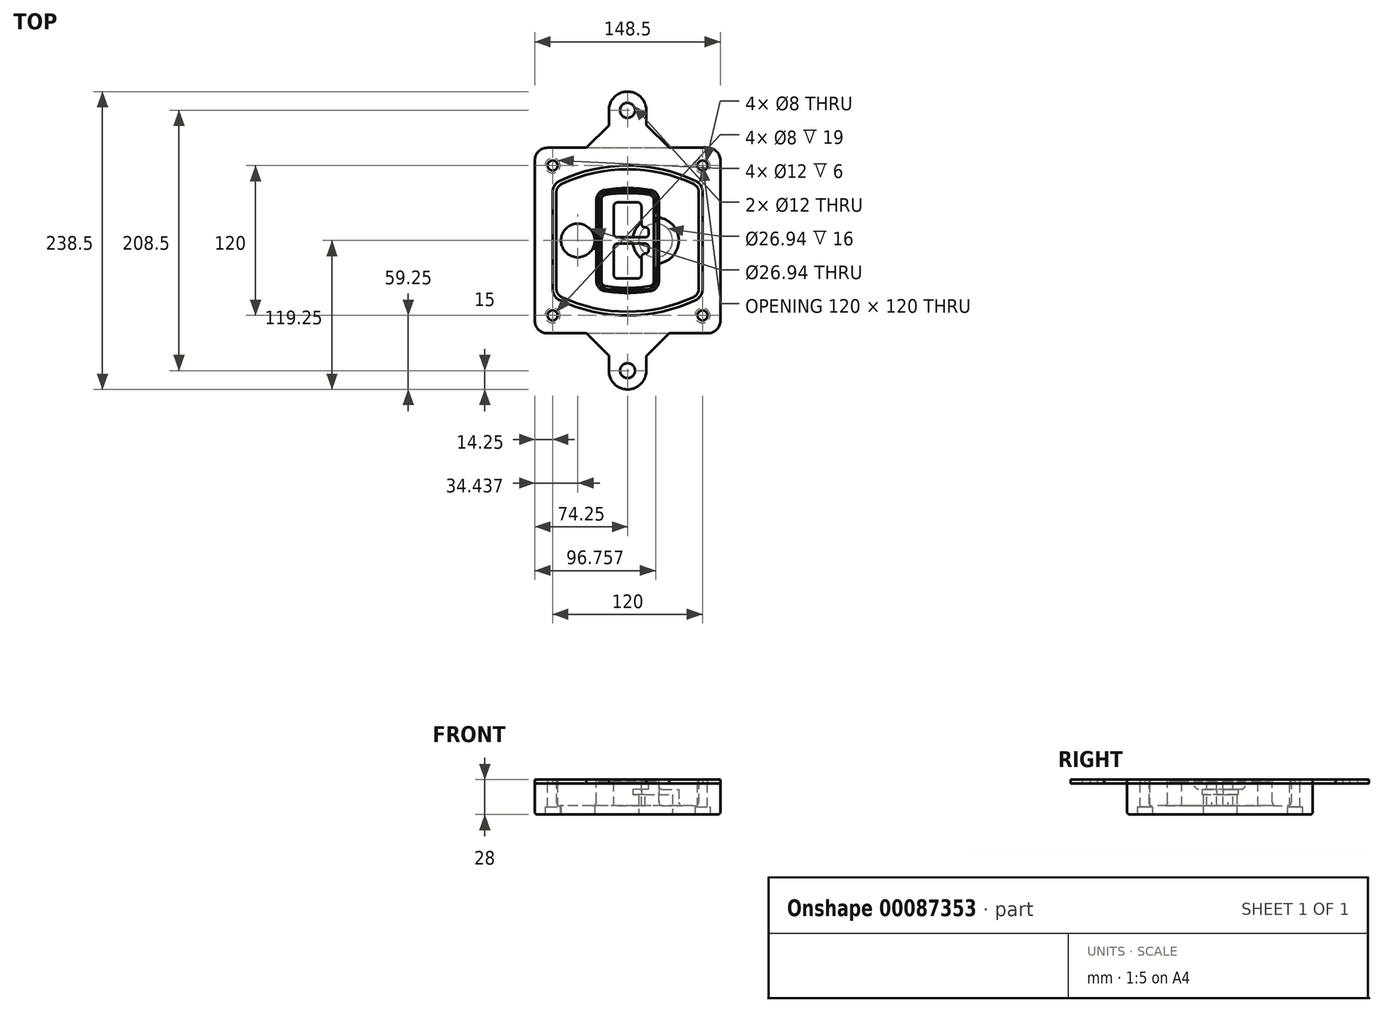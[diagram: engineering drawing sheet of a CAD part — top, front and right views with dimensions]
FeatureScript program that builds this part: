
annotation { "Feature Type Name" : "Feature", "Feature Type Description" : "" }
export const myFeature = defineFeature(function(context is Context, id is Id, definition is map)
    precondition{}
    {
        {
            var Q0;
            Q0=qCreatedBy(makeId("Top.planeOp"),FACE);
            var sketch = newSketch(context, id + "F0", { "sketchPlane" : qUnion([Q0])});
            skPoint(sketch, "E0.rect.middle", {"position": v(0, 0) * mm});
            skLineSegment(sketch, "E1.bottom", {"start": v(-64.25, -74.25) * mm, "end": v(64.25, -74.25) * mm});
            skLineSegment(sketch, "E1.top", {"start": v(-64.25, 74.25) * mm, "end": v(64.25, 74.25) * mm});
            skLineSegment(sketch, "E1.left", {"start": v(-74.25, -64.25) * mm, "end": v(-74.25, 64.25) * mm});
            skLineSegment(sketch, "E1.right", {"start": v(74.25, -64.25) * mm, "end": v(74.25, 64.25) * mm});
            skLineSegment(sketch, "E2", {"start": v(-74.25, 74.25) * mm, "end": v(74.25, -74.25) * mm, "construction": true});
            skLineSegment(sketch, "E3", {"start": v(74.25, 74.25) * mm, "end": v(-74.25, -74.25) * mm, "construction": true});
            skCircle(sketch, "E4", {"center": v(-60, 60) * mm, "radius": 4 * mm});
            skCircle(sketch, "E5", {"center": v(60, 60) * mm, "radius": 4 * mm});
            skCircle(sketch, "E6", {"center": v(60, -60) * mm, "radius": 4 * mm});
            skCircle(sketch, "E7", {"center": v(-60, -60) * mm, "radius": 4 * mm});
            skLineSegment(sketch, "E8", {"start": v(-60, 60) * mm, "end": v(60, 60) * mm, "construction": true});
            skLineSegment(sketch, "E9", {"start": v(60, 60) * mm, "end": v(60, -60) * mm, "construction": true});
            skLineSegment(sketch, "E10", {"start": v(60, -60) * mm, "end": v(-60, -60) * mm, "construction": true});
            skLineSegment(sketch, "E11", {"start": v(-60, -60) * mm, "end": v(-60, 60) * mm, "construction": true});
            skLineSegment(sketch, "E12", {"start": v(-60, 38.83) * mm, "end": v(-60, -38.83) * mm});
            skLineSegment(sketch, "E13", {"start": v(60, 38.83) * mm, "end": v(60, -38.83) * mm});
            skArc(sketch, "E14", {"start": v(54.26, 47.88) * mm, "mid": v(0, 60) * mm, "end": v(-54.26, 47.88) * mm});
            skArc(sketch, "E15", {"start": v(-54.26, -47.88) * mm, "mid": v(0, -60) * mm, "end": v(54.26, -47.88) * mm});
            skLineSegment(sketch, "E16", {"start": v(-60, 0) * mm, "end": v(60, 0) * mm, "construction": true});
            skPoint(sketch, "E17.visualSharp", {"position": v(-60, -45) * mm});
            skArc(sketch, "E17.filletArc", {"start": v(-60, -38.83) * mm, "mid": v(-58.44, -44.2) * mm, "end": v(-54.26, -47.88) * mm});
            skPoint(sketch, "E18.visualSharp", {"position": v(-60, 45) * mm});
            skArc(sketch, "E18.filletArc", {"start": v(-54.26, 47.88) * mm, "mid": v(-58.44, 44.2) * mm, "end": v(-60, 38.83) * mm});
            skPoint(sketch, "E19.visualSharp", {"position": v(60, 45) * mm});
            skArc(sketch, "E19.filletArc", {"start": v(60, 38.83) * mm, "mid": v(58.44, 44.2) * mm, "end": v(54.26, 47.88) * mm});
            skPoint(sketch, "E20.visualSharp", {"position": v(60, -45) * mm});
            skArc(sketch, "E20.filletArc", {"start": v(54.26, -47.88) * mm, "mid": v(58.44, -44.2) * mm, "end": v(60, -38.83) * mm});
            skPoint(sketch, "E21.visualSharp", {"position": v(-74.25, 74.25) * mm});
            skArc(sketch, "E21.filletArc", {"start": v(-64.25, 74.25) * mm, "mid": v(-71.32, 71.32) * mm, "end": v(-74.25, 64.25) * mm});
            skPoint(sketch, "E22.visualSharp", {"position": v(74.25, 74.25) * mm});
            skArc(sketch, "E22.filletArc", {"start": v(74.25, 64.25) * mm, "mid": v(71.32, 71.32) * mm, "end": v(64.25, 74.25) * mm});
            skPoint(sketch, "E23.visualSharp", {"position": v(74.25, -74.25) * mm});
            skArc(sketch, "E23.filletArc", {"start": v(64.25, -74.25) * mm, "mid": v(71.32, -71.32) * mm, "end": v(74.25, -64.25) * mm});
            skPoint(sketch, "E24.visualSharp", {"position": v(-74.25, -74.25) * mm});
            skArc(sketch, "E24.filletArc", {"start": v(-74.25, -64.25) * mm, "mid": v(-71.32, -71.32) * mm, "end": v(-64.25, -74.25) * mm});
            skArc(sketch, "E25.0", {"start": v(57, 38.83) * mm, "mid": v(55.9, 42.58) * mm, "end": v(52.98, 45.17) * mm});
            skLineSegment(sketch, "E25.1", {"start": v(57, 38.83) * mm, "end": v(57, -38.83) * mm});
            skArc(sketch, "E25.2", {"start": v(52.98, -45.17) * mm, "mid": v(55.9, -42.58) * mm, "end": v(57, -38.83) * mm});
            skArc(sketch, "E25.3", {"start": v(-52.98, -45.17) * mm, "mid": v(0, -57) * mm, "end": v(52.98, -45.17) * mm});
            skArc(sketch, "E25.4", {"start": v(-57, -38.83) * mm, "mid": v(-55.9, -42.58) * mm, "end": v(-52.98, -45.17) * mm});
            skArc(sketch, "E25.5", {"start": v(52.98, 45.17) * mm, "mid": v(0, 57) * mm, "end": v(-52.98, 45.17) * mm});
            skLineSegment(sketch, "E25.6", {"start": v(-57, 38.83) * mm, "end": v(-57, -38.83) * mm});
            skArc(sketch, "E25.7", {"start": v(-52.98, 45.17) * mm, "mid": v(-55.9, 42.58) * mm, "end": v(-57, 38.83) * mm});
            skArc(sketch, "E26.0", {"start": v(-55.96, 51.5) * mm, "mid": v(-61.82, 46.33) * mm, "end": v(-64, 38.83) * mm});
            skArc(sketch, "E26.1", {"start": v(55.96, 51.5) * mm, "mid": v(0, 64) * mm, "end": v(-55.96, 51.5) * mm});
            skArc(sketch, "E26.2", {"start": v(64, 38.83) * mm, "mid": v(61.82, 46.33) * mm, "end": v(55.96, 51.5) * mm});
            skLineSegment(sketch, "E26.3", {"start": v(64, 38.83) * mm, "end": v(64, -38.83) * mm});
            skArc(sketch, "E26.4", {"start": v(55.96, -51.5) * mm, "mid": v(61.82, -46.33) * mm, "end": v(64, -38.83) * mm});
            skLineSegment(sketch, "E26.5", {"start": v(-64, 38.83) * mm, "end": v(-64, -38.83) * mm});
            skArc(sketch, "E26.6", {"start": v(-55.96, -51.5) * mm, "mid": v(0, -64) * mm, "end": v(55.96, -51.5) * mm});
            skArc(sketch, "E26.7", {"start": v(-64, -38.83) * mm, "mid": v(-61.82, -46.33) * mm, "end": v(-55.96, -51.5) * mm});
            skSolve(sketch);
        }
        {
            var Q0;
            Q0=makeQuery(id+"F0.imprint","IMPRINT",FACE,{"disambiguationData":[TD([[makeQuery(id+"F0.imprint","IMPRINT",EDGE,{"derivedFrom":sQuery(id+"F0.wireOp",EDGE,"E1.bottom")}),1.0]])]});
            var Q1;
            Q1=makeQuery(id+"F0.imprint","IMPRINT",FACE,{"disambiguationData":[TD([[makeQuery(id+"F0.imprint","IMPRINT",EDGE,{"derivedFrom":sQuery(id+"F0.wireOp",EDGE,"E12")}),1.0]])]});
            var Q2;
            Q2=makeQuery(id+"F0.imprint","IMPRINT",FACE,{"disambiguationData":[TD([[makeQuery(id+"F0.imprint","IMPRINT",EDGE,{"derivedFrom":sQuery(id+"F0.wireOp",EDGE,"E25.0")}),1.0]])]});
            var Q3;
            Q3=makeQuery(id+"F0.imprint","IMPRINT",FACE,{"disambiguationData":[TD([[makeQuery(id+"F0.imprint","IMPRINT",EDGE,{"derivedFrom":sQuery(id+"F0.wireOp",EDGE,"E12")}),-1.0]])]});
            extrude(context, id + "F1", {"entities" : qUnion([Q0, Q1, Q2, Q3]), "oppositeDirection" : true, "depth" : 25 * mm});
        }
        {
            var Q0;
            Q0=makeQuery(id+"F0.imprint","IMPRINT",FACE,{"disambiguationData":[TD([[makeQuery(id+"F0.imprint","IMPRINT",EDGE,{"derivedFrom":sQuery(id+"F0.wireOp",EDGE,"E12")}),1.0]])]});
            extrude(context, id + "F2", {"entities" : qUnion([Q0]), "operationType" : NewBodyOperationType.ADD, "depth" : 3 * mm});
        }
        {
            var Q0;
            Q0=makeQuery(id+"F0.imprint","IMPRINT",FACE,{"disambiguationData":[TD([[makeQuery(id+"F0.imprint","IMPRINT",EDGE,{"derivedFrom":sQuery(id+"F0.wireOp",EDGE,"E25.0")}),1.0]])]});
            extrude(context, id + "F3", {"entities" : qUnion([Q0]), "operationType" : NewBodyOperationType.REMOVE, "oppositeDirection" : true, "depth" : 18 * mm});
        }
        {
            var Q0;
            Q0=makeQuery(id+"F2.opExtrude","CAP_FACE",FACE,{"disambiguationData":[OSD([sQuery(id+"F0.wireOp",EDGE,"E12"),sQuery(id+"F0.wireOp",EDGE,"E13"),sQuery(id+"F0.wireOp",EDGE,"E14"),sQuery(id+"F0.wireOp",EDGE,"E15"),sQuery(id+"F0.wireOp",EDGE,"E17.filletArc"),sQuery(id+"F0.wireOp",EDGE,"E18.filletArc"),sQuery(id+"F0.wireOp",EDGE,"E19.filletArc"),sQuery(id+"F0.wireOp",EDGE,"E20.filletArc"),sQuery(id+"F0.wireOp",EDGE,"E25.0"),sQuery(id+"F0.wireOp",EDGE,"E25.1"),sQuery(id+"F0.wireOp",EDGE,"E25.2"),sQuery(id+"F0.wireOp",EDGE,"E25.3"),sQuery(id+"F0.wireOp",EDGE,"E25.4"),sQuery(id+"F0.wireOp",EDGE,"E25.5"),sQuery(id+"F0.wireOp",EDGE,"E25.6"),sQuery(id+"F0.wireOp",EDGE,"E25.7")])],"isStart":false});
            var sketch = newSketch(context, id + "F4", { "sketchPlane" : qUnion([Q0])});
            skArc(sketch, "E27.0", {"start": v(-18.34, -40.45) * mm, "mid": v(0, -42) * mm, "end": v(18.34, -40.45) * mm});
            skArc(sketch, "E28.0", {"start": v(18.34, 40.45) * mm, "mid": v(0, 42) * mm, "end": v(-18.34, 40.45) * mm});
            skLineSegment(sketch, "E29", {"start": v(-25, 32.57) * mm, "end": v(-25, -32.57) * mm});
            skLineSegment(sketch, "E30", {"start": v(25, 32.57) * mm, "end": v(25, -32.57) * mm});
            skLineSegment(sketch, "E31", {"start": v(-25, 39.1) * mm, "end": v(25, 39.1) * mm, "construction": true});
            skLineSegment(sketch, "E32", {"start": v(-25, -39.1) * mm, "end": v(25, -39.1) * mm, "construction": true});
            skPoint(sketch, "E33.visualSharp", {"position": v(-25, 39.1) * mm});
            skArc(sketch, "E33.filletArc", {"start": v(-18.34, 40.45) * mm, "mid": v(-23.11, 37.73) * mm, "end": v(-25, 32.57) * mm});
            skPoint(sketch, "E34.visualSharp", {"position": v(25, 39.1) * mm});
            skArc(sketch, "E34.filletArc", {"start": v(25, 32.57) * mm, "mid": v(23.11, 37.73) * mm, "end": v(18.34, 40.45) * mm});
            skPoint(sketch, "E35.visualSharp", {"position": v(25, -39.1) * mm});
            skArc(sketch, "E35.filletArc", {"start": v(18.34, -40.45) * mm, "mid": v(23.11, -37.73) * mm, "end": v(25, -32.57) * mm});
            skPoint(sketch, "E36.visualSharp", {"position": v(-25, -39.1) * mm});
            skArc(sketch, "E36.filletArc", {"start": v(-25, -32.57) * mm, "mid": v(-23.11, -37.73) * mm, "end": v(-18.34, -40.45) * mm});
            skArc(sketch, "E37.0", {"start": v(52.98, 45.17) * mm, "mid": v(0, 57) * mm, "end": v(-52.98, 45.17) * mm});
            skArc(sketch, "E37.1", {"start": v(-52.98, 45.17) * mm, "mid": v(-55.9, 42.58) * mm, "end": v(-57, 38.83) * mm});
            skLineSegment(sketch, "E37.2", {"start": v(-57, 38.83) * mm, "end": v(-57, -38.83) * mm});
            skArc(sketch, "E37.3", {"start": v(-57, -38.83) * mm, "mid": v(-55.9, -42.58) * mm, "end": v(-52.98, -45.17) * mm});
            skArc(sketch, "E37.4", {"start": v(-52.98, -45.17) * mm, "mid": v(0, -57) * mm, "end": v(52.98, -45.17) * mm});
            skArc(sketch, "E37.5", {"start": v(52.98, -45.17) * mm, "mid": v(55.9, -42.58) * mm, "end": v(57, -38.83) * mm});
            skLineSegment(sketch, "E37.6", {"start": v(57, 38.83) * mm, "end": v(57, -38.83) * mm});
            skArc(sketch, "E37.7", {"start": v(57, 38.83) * mm, "mid": v(55.9, 42.58) * mm, "end": v(52.98, 45.17) * mm});
            skLineSegment(sketch, "E38.0", {"start": v(23, 32.57) * mm, "end": v(23, -32.57) * mm});
            skArc(sketch, "E38.1", {"start": v(18, -38.48) * mm, "mid": v(21.58, -36.44) * mm, "end": v(23, -32.57) * mm});
            skArc(sketch, "E38.2", {"start": v(-18, -38.48) * mm, "mid": v(0, -40) * mm, "end": v(18, -38.48) * mm});
            skArc(sketch, "E38.3", {"start": v(-23, -32.57) * mm, "mid": v(-21.58, -36.44) * mm, "end": v(-18, -38.48) * mm});
            skLineSegment(sketch, "E38.4", {"start": v(-23, 32.57) * mm, "end": v(-23, -32.57) * mm});
            skArc(sketch, "E38.5", {"start": v(23, 32.57) * mm, "mid": v(21.58, 36.44) * mm, "end": v(18, 38.48) * mm});
            skArc(sketch, "E38.6", {"start": v(-18, 38.48) * mm, "mid": v(-21.58, 36.44) * mm, "end": v(-23, 32.57) * mm});
            skArc(sketch, "E38.7", {"start": v(18, 38.48) * mm, "mid": v(0, 40) * mm, "end": v(-18, 38.48) * mm});
            skArc(sketch, "E39.0", {"start": v(21, 32.57) * mm, "mid": v(20.06, 35.15) * mm, "end": v(17.67, 36.5) * mm});
            skLineSegment(sketch, "E39.1", {"start": v(21, 32.57) * mm, "end": v(21, -32.57) * mm});
            skArc(sketch, "E39.2", {"start": v(17.67, -36.5) * mm, "mid": v(20.06, -35.15) * mm, "end": v(21, -32.57) * mm});
            skArc(sketch, "E39.3", {"start": v(-17.67, -36.5) * mm, "mid": v(0, -38) * mm, "end": v(17.67, -36.5) * mm});
            skArc(sketch, "E39.4", {"start": v(-21, -32.57) * mm, "mid": v(-20.06, -35.15) * mm, "end": v(-17.67, -36.5) * mm});
            skArc(sketch, "E39.5", {"start": v(17.67, 36.5) * mm, "mid": v(0, 38) * mm, "end": v(-17.67, 36.5) * mm});
            skLineSegment(sketch, "E39.6", {"start": v(-21, 32.57) * mm, "end": v(-21, -32.57) * mm});
            skArc(sketch, "E39.7", {"start": v(-17.67, 36.5) * mm, "mid": v(-20.06, 35.15) * mm, "end": v(-21, 32.57) * mm});
            skLineSegment(sketch, "E40", {"start": v(-25, 0) * mm, "end": v(25, 0) * mm, "construction": true});
            skLineSegment(sketch, "E41", {"start": v(-11, 5.5) * mm, "end": v(-11, 27.5) * mm});
            skLineSegment(sketch, "E42", {"start": v(-8, 30.5) * mm, "end": v(8, 30.5) * mm});
            skLineSegment(sketch, "E43", {"start": v(11, 27.5) * mm, "end": v(11, 13.5) * mm});
            skLineSegment(sketch, "E44", {"start": v(14, 10.5) * mm, "end": v(14, 10.5) * mm});
            skLineSegment(sketch, "E45", {"start": v(17, 7.5) * mm, "end": v(17, 5.5) * mm});
            skLineSegment(sketch, "E46", {"start": v(14, 2.5) * mm, "end": v(-8, 2.5) * mm});
            skPoint(sketch, "E47.visualSharp", {"position": v(-11, 30.5) * mm});
            skArc(sketch, "E47.filletArc", {"start": v(-8, 30.5) * mm, "mid": v(-10.12, 29.62) * mm, "end": v(-11, 27.5) * mm});
            skPoint(sketch, "E48.visualSharp", {"position": v(11, 30.5) * mm});
            skArc(sketch, "E48.filletArc", {"start": v(11, 27.5) * mm, "mid": v(10.12, 29.62) * mm, "end": v(8, 30.5) * mm});
            skPoint(sketch, "E49.visualSharp", {"position": v(11, 10.5) * mm});
            skArc(sketch, "E49.filletArc", {"start": v(11, 13.5) * mm, "mid": v(11.88, 11.38) * mm, "end": v(14, 10.5) * mm});
            skPoint(sketch, "E50.visualSharp", {"position": v(17, 10.5) * mm});
            skArc(sketch, "E50.filletArc", {"start": v(17, 7.5) * mm, "mid": v(16.12, 9.62) * mm, "end": v(14, 10.5) * mm});
            skPoint(sketch, "E51.visualSharp", {"position": v(17, 2.5) * mm});
            skArc(sketch, "E51.filletArc", {"start": v(14, 2.5) * mm, "mid": v(16.12, 3.38) * mm, "end": v(17, 5.5) * mm});
            skPoint(sketch, "E52.visualSharp", {"position": v(-11, 2.5) * mm});
            skArc(sketch, "E52.filletArc", {"start": v(-11, 5.5) * mm, "mid": v(-10.12, 3.38) * mm, "end": v(-8, 2.5) * mm});
            skLineSegment(sketch, "E53.0.MirrorCS", {"start": v(14, -2.5) * mm, "end": v(-8, -2.5) * mm});
            skArc(sketch, "E54.0.MirrorCS", {"start": v(-11, -5.5) * mm, "mid": v(-10.12, -3.38) * mm, "end": v(-8, -2.5) * mm});
            skLineSegment(sketch, "E55.0.MirrorCS", {"start": v(-11, -5.5) * mm, "end": v(-11, -27.5) * mm});
            skArc(sketch, "E56.0.MirrorCS", {"start": v(-8, -30.5) * mm, "mid": v(-10.12, -29.62) * mm, "end": v(-11, -27.5) * mm});
            skLineSegment(sketch, "E57.0.MirrorCS", {"start": v(-8, -30.5) * mm, "end": v(8, -30.5) * mm});
            skArc(sketch, "E58.0.MirrorCS", {"start": v(11, -27.5) * mm, "mid": v(10.12, -29.62) * mm, "end": v(8, -30.5) * mm});
            skLineSegment(sketch, "E59.0.MirrorCS", {"start": v(11, -27.5) * mm, "end": v(11, -13.5) * mm});
            skArc(sketch, "E60.0.MirrorCS", {"start": v(11, -13.5) * mm, "mid": v(11.88, -11.38) * mm, "end": v(14, -10.5) * mm});
            skArc(sketch, "E61.0.MirrorCS", {"start": v(17, -7.5) * mm, "mid": v(16.12, -9.62) * mm, "end": v(14, -10.5) * mm});
            skLineSegment(sketch, "E62.0.MirrorCS", {"start": v(17, -7.5) * mm, "end": v(17, -5.5) * mm});
            skArc(sketch, "E63.0.MirrorCS", {"start": v(14, -2.5) * mm, "mid": v(16.12, -3.38) * mm, "end": v(17, -5.5) * mm});
            skSolve(sketch);
        }
        {
            var Q0;
            Q0=makeQuery(id+"F4.imprint","IMPRINT",FACE,{"disambiguationData":[TD([[makeQuery(id+"F4.imprint","IMPRINT",EDGE,{"derivedFrom":sQuery(id+"F4.wireOp",EDGE,"E27.0")}),1.0]])]});
            var Q1;
            Q1=makeQuery(id+"F4.imprint","IMPRINT",FACE,{"disambiguationData":[TD([[makeQuery(id+"F4.imprint","IMPRINT",EDGE,{"derivedFrom":sQuery(id+"F4.wireOp",EDGE,"E38.0")}),-1.0]])]});
            var Q2;
            Q2=makeQuery(id+"F4.imprint","IMPRINT",FACE,{"disambiguationData":[TD([[makeQuery(id+"F4.imprint","IMPRINT",EDGE,{"derivedFrom":sQuery(id+"F4.wireOp",EDGE,"E39.0")}),1.0]])]});
            extrude(context, id + "F5", {"entities" : qUnion([Q0, Q1, Q2]), "operationType" : NewBodyOperationType.ADD, "endBound" : BoundingType.UP_TO_NEXT, "oppositeDirection" : true, "depth" : 25 * mm});
        }
        {
            var Q0;
            Q0=makeQuery(id+"F4.imprint","IMPRINT",FACE,{"disambiguationData":[TD([[makeQuery(id+"F4.imprint","IMPRINT",EDGE,{"derivedFrom":sQuery(id+"F4.wireOp",EDGE,"E38.0")}),-1.0]])]});
            extrude(context, id + "F6", {"entities" : qUnion([Q0]), "operationType" : NewBodyOperationType.REMOVE, "oppositeDirection" : true, "depth" : 2 * mm});
        }
        {
            var Q0;
            Q0=makeQuery(id+"F1.opExtrude","CAP_FACE",FACE,{"disambiguationData":[OSD([sQuery(id+"F0.wireOp",EDGE,"E1.bottom"),sQuery(id+"F0.wireOp",EDGE,"E1.top"),sQuery(id+"F0.wireOp",EDGE,"E1.left"),sQuery(id+"F0.wireOp",EDGE,"E1.right"),sQuery(id+"F0.wireOp",EDGE,"E4"),sQuery(id+"F0.wireOp",EDGE,"E5"),sQuery(id+"F0.wireOp",EDGE,"E6"),sQuery(id+"F0.wireOp",EDGE,"E7"),sQuery(id+"F0.wireOp",EDGE,"E21.filletArc"),sQuery(id+"F0.wireOp",EDGE,"E22.filletArc"),sQuery(id+"F0.wireOp",EDGE,"E23.filletArc"),sQuery(id+"F0.wireOp",EDGE,"E24.filletArc")])],"isStart":false});
            var sketch = newSketch(context, id + "F7", { "sketchPlane" : qUnion([Q0])});
            skCircle(sketch, "E64", {"center": v(22.5, 0) * mm, "radius": 13.47 * mm});
            skCircle(sketch, "E65", {"center": v(-39.81, 0) * mm, "radius": 13.47 * mm});
            skLineSegment(sketch, "E66", {"start": v(74.25, 0) * mm, "end": v(-74.25, 0) * mm});
            skCircle(sketch, "E67", {"center": v(22.5, 0) * mm, "radius": 18.47 * mm});
            skCircle(sketch, "E68", {"center": v(60, -60) * mm, "radius": 6 * mm});
            skCircle(sketch, "E69", {"center": v(-60, -60) * mm, "radius": 6 * mm});
            skCircle(sketch, "E70", {"center": v(-60, 60) * mm, "radius": 6 * mm});
            skCircle(sketch, "E71", {"center": v(60, 60) * mm, "radius": 6 * mm});
            skSolve(sketch);
        }
        {
            var Q0;
            {var subQ1=sQuery(id+"F7.wireOp",EDGE,"E66");var subQ4=sQuery(id+"F7.wireOp",EDGE,"E64");var subQ6=makeQuery(id+"F7.imprint","INTERSECT",VERTEX,{"disambiguationData":[OD(0.0)],"derivedFrom":[subQ4,subQ1]});Q0=makeQuery(id+"F7.imprint","IMPRINT",FACE,{"disambiguationData":[TD([[makeQuery(id+"F7.imprint","IMPRINT",EDGE,{"disambiguationData":[TD([[subQ6,-1.0]])],"derivedFrom":subQ4}),-1.0]])]});}
            var Q1;
            {var subQ0=sQuery(id+"F7.wireOp",EDGE,"E66");var subQ1=sQuery(id+"F7.wireOp",EDGE,"E64");var subQ3=makeQuery(id+"F7.imprint","INTERSECT",VERTEX,{"disambiguationData":[OD(0.0)],"derivedFrom":[subQ1,subQ0]});Q1=makeQuery(id+"F7.imprint","IMPRINT",FACE,{"disambiguationData":[TD([[makeQuery(id+"F7.imprint","IMPRINT",EDGE,{"disambiguationData":[TD([[subQ3,-1.0]])],"derivedFrom":subQ1}),1.0]])]});}
            var Q2;
            {var subQ0=sQuery(id+"F7.wireOp",EDGE,"E66");var subQ1=sQuery(id+"F7.wireOp",EDGE,"E64");var subQ3=makeQuery(id+"F7.imprint","INTERSECT",VERTEX,{"disambiguationData":[OD(0.0)],"derivedFrom":[subQ1,subQ0]});Q2=makeQuery(id+"F7.imprint","IMPRINT",FACE,{"disambiguationData":[TD([[makeQuery(id+"F7.imprint","IMPRINT",EDGE,{"disambiguationData":[TD([[subQ3,1.0]])],"derivedFrom":subQ1}),1.0]])]});}
            var Q3;
            {var subQ1=sQuery(id+"F7.wireOp",EDGE,"E66");var subQ4=sQuery(id+"F7.wireOp",EDGE,"E64");var subQ6=makeQuery(id+"F7.imprint","INTERSECT",VERTEX,{"disambiguationData":[OD(0.0)],"derivedFrom":[subQ4,subQ1]});Q3=makeQuery(id+"F7.imprint","IMPRINT",FACE,{"disambiguationData":[TD([[makeQuery(id+"F7.imprint","IMPRINT",EDGE,{"disambiguationData":[TD([[subQ6,1.0]])],"derivedFrom":subQ4}),-1.0]])]});}
            extrude(context, id + "F8", {"entities" : qUnion([Q0, Q1, Q2, Q3]), "operationType" : NewBodyOperationType.ADD, "oppositeDirection" : true, "depth" : 20 * mm});
        }
        {
            var Q0;
            {var subQ0=sQuery(id+"F7.wireOp",EDGE,"E66");var subQ1=sQuery(id+"F7.wireOp",EDGE,"E64");var subQ3=makeQuery(id+"F7.imprint","INTERSECT",VERTEX,{"disambiguationData":[OD(0.0)],"derivedFrom":[subQ1,subQ0]});Q0=makeQuery(id+"F7.imprint","IMPRINT",FACE,{"disambiguationData":[TD([[makeQuery(id+"F7.imprint","IMPRINT",EDGE,{"disambiguationData":[TD([[subQ3,-1.0]])],"derivedFrom":subQ1}),1.0]])]});}
            var Q1;
            {var subQ0=sQuery(id+"F7.wireOp",EDGE,"E66");var subQ1=sQuery(id+"F7.wireOp",EDGE,"E64");var subQ3=makeQuery(id+"F7.imprint","INTERSECT",VERTEX,{"disambiguationData":[OD(0.0)],"derivedFrom":[subQ1,subQ0]});Q1=makeQuery(id+"F7.imprint","IMPRINT",FACE,{"disambiguationData":[TD([[makeQuery(id+"F7.imprint","IMPRINT",EDGE,{"disambiguationData":[TD([[subQ3,1.0]])],"derivedFrom":subQ1}),1.0]])]});}
            extrude(context, id + "F9", {"entities" : qUnion([Q0, Q1]), "operationType" : NewBodyOperationType.REMOVE, "oppositeDirection" : true, "depth" : 16 * mm});
        }
        {
            var Q0;
            {var subQ0=sQuery(id+"F7.wireOp",EDGE,"E66");var subQ1=sQuery(id+"F7.wireOp",EDGE,"E65");var subQ3=makeQuery(id+"F7.imprint","INTERSECT",VERTEX,{"disambiguationData":[OD(0.0)],"derivedFrom":[subQ1,subQ0]});Q0=makeQuery(id+"F7.imprint","IMPRINT",FACE,{"disambiguationData":[TD([[makeQuery(id+"F7.imprint","IMPRINT",EDGE,{"disambiguationData":[TD([[subQ3,-1.0]])],"derivedFrom":subQ1}),1.0]])]});}
            var Q1;
            {var subQ0=sQuery(id+"F7.wireOp",EDGE,"E66");var subQ1=sQuery(id+"F7.wireOp",EDGE,"E65");var subQ3=makeQuery(id+"F7.imprint","INTERSECT",VERTEX,{"disambiguationData":[OD(0.0)],"derivedFrom":[subQ1,subQ0]});Q1=makeQuery(id+"F7.imprint","IMPRINT",FACE,{"disambiguationData":[TD([[makeQuery(id+"F7.imprint","IMPRINT",EDGE,{"disambiguationData":[TD([[subQ3,1.0]])],"derivedFrom":subQ1}),1.0]])]});}
            extrude(context, id + "F10", {"entities" : qUnion([Q0, Q1]), "operationType" : NewBodyOperationType.REMOVE, "oppositeDirection" : true, "depth" : 25 * mm});
        }
        {
            var Q0;
            Q0=makeQuery(id+"F7.imprint","IMPRINT",FACE,{"disambiguationData":[TD([[makeQuery(id+"F7.imprint","IMPRINT",EDGE,{"derivedFrom":sQuery(id+"F7.wireOp",EDGE,"E68")}),1.0]])]});
            var Q1;
            Q1=makeQuery(id+"F7.imprint","IMPRINT",FACE,{"disambiguationData":[TD([[makeQuery(id+"F7.imprint","IMPRINT",EDGE,{"derivedFrom":makeQuery(id+"F1.opExtrude","CAP_EDGE",EDGE,{"disambiguationData":[OSD([sQuery(id+"F0.wireOp",EDGE,"E5")])],"isStart":false})}),-1.0]])]});
            var Q2;
            Q2=makeQuery(id+"F7.imprint","IMPRINT",FACE,{"disambiguationData":[TD([[makeQuery(id+"F7.imprint","IMPRINT",EDGE,{"derivedFrom":sQuery(id+"F7.wireOp",EDGE,"E69")}),1.0]])]});
            var Q3;
            Q3=makeQuery(id+"F7.imprint","IMPRINT",FACE,{"disambiguationData":[TD([[makeQuery(id+"F7.imprint","IMPRINT",EDGE,{"derivedFrom":makeQuery(id+"F1.opExtrude","CAP_EDGE",EDGE,{"disambiguationData":[OSD([sQuery(id+"F0.wireOp",EDGE,"E4")])],"isStart":false})}),-1.0]])]});
            var Q4;
            Q4=makeQuery(id+"F7.imprint","IMPRINT",FACE,{"disambiguationData":[TD([[makeQuery(id+"F7.imprint","IMPRINT",EDGE,{"derivedFrom":sQuery(id+"F7.wireOp",EDGE,"E70")}),1.0]])]});
            var Q5;
            Q5=makeQuery(id+"F7.imprint","IMPRINT",FACE,{"disambiguationData":[TD([[makeQuery(id+"F7.imprint","IMPRINT",EDGE,{"derivedFrom":makeQuery(id+"F1.opExtrude","CAP_EDGE",EDGE,{"disambiguationData":[OSD([sQuery(id+"F0.wireOp",EDGE,"E7")])],"isStart":false})}),-1.0]])]});
            var Q6;
            Q6=makeQuery(id+"F7.imprint","IMPRINT",FACE,{"disambiguationData":[TD([[makeQuery(id+"F7.imprint","IMPRINT",EDGE,{"derivedFrom":sQuery(id+"F7.wireOp",EDGE,"E71")}),1.0]])]});
            var Q7;
            Q7=makeQuery(id+"F7.imprint","IMPRINT",FACE,{"disambiguationData":[TD([[makeQuery(id+"F7.imprint","IMPRINT",EDGE,{"derivedFrom":makeQuery(id+"F1.opExtrude","CAP_EDGE",EDGE,{"disambiguationData":[OSD([sQuery(id+"F0.wireOp",EDGE,"E6")])],"isStart":false})}),-1.0]])]});
            extrude(context, id + "F11", {"entities" : qUnion([Q0, Q1, Q2, Q3, Q4, Q5, Q6, Q7]), "operationType" : NewBodyOperationType.REMOVE, "oppositeDirection" : true, "depth" : 6 * mm});
        }
        {
            var Q0;
            Q0=makeQuery(id+"F9.boolean.opBoolean","COPY",FACE,{"derivedFrom":makeQuery(id+"F9.opExtrude","CAP_FACE",FACE,{"disambiguationData":[OSD([sQuery(id+"F7.wireOp",EDGE,"E64")])],"isStart":false})});
            var sketch = newSketch(context, id + "F12", { "sketchPlane" : qUnion([Q0])});
            skArc(sketch, "E72.0", {"start": v(11, 14.45) * mm, "mid": v(6.45, 9.13) * mm, "end": v(4.2, 2.5) * mm});
            skArc(sketch, "E72.1", {"start": v(4.2, -2.5) * mm, "mid": v(6.45, -9.13) * mm, "end": v(11, -14.45) * mm});
            skLineSegment(sketch, "E73", {"start": v(4.2, -2.5) * mm, "end": v(14, -2.5) * mm});
            skLineSegment(sketch, "E74.0", {"start": v(14, 2.5) * mm, "end": v(4.2, 2.5) * mm});
            skArc(sketch, "E74.1", {"start": v(14, 2.5) * mm, "mid": v(16.12, 3.38) * mm, "end": v(17, 5.5) * mm});
            skLineSegment(sketch, "E74.2", {"start": v(17, 7.5) * mm, "end": v(17, 5.5) * mm});
            skArc(sketch, "E74.3", {"start": v(17, 7.5) * mm, "mid": v(16.12, 9.62) * mm, "end": v(14, 10.5) * mm});
            skArc(sketch, "E74.4", {"start": v(11, 13.5) * mm, "mid": v(11.88, 11.38) * mm, "end": v(14, 10.5) * mm});
            skLineSegment(sketch, "E74.5", {"start": v(11, 14.45) * mm, "end": v(11, 13.5) * mm});
            skLineSegment(sketch, "E74.7", {"start": v(14, -2.5) * mm, "end": v(4.2, -2.5) * mm});
            skArc(sketch, "E74.8", {"start": v(14, -2.5) * mm, "mid": v(16.12, -3.38) * mm, "end": v(17, -5.5) * mm});
            skLineSegment(sketch, "E74.9", {"start": v(17, -7.5) * mm, "end": v(17, -5.5) * mm});
            skArc(sketch, "E74.10", {"start": v(17, -7.5) * mm, "mid": v(16.12, -9.62) * mm, "end": v(14, -10.5) * mm});
            skArc(sketch, "E74.11", {"start": v(11, -13.5) * mm, "mid": v(11.88, -11.38) * mm, "end": v(14, -10.5) * mm});
            skLineSegment(sketch, "E74.12", {"start": v(11, -14.45) * mm, "end": v(11, -13.5) * mm});
            skPoint(sketch, "E75.orphan", {"position": v(11, -27.5) * mm});
            skPoint(sketch, "E76.orphan", {"position": v(-8, -2.5) * mm});
            skPoint(sketch, "E77.orphan", {"position": v(-8, 2.5) * mm});
            skPoint(sketch, "E78.orphan", {"position": v(11, 27.5) * mm});
            skSolve(sketch);
        }
        {
            var Q0;
            {var subQ7=sQuery(id+"F12.wireOp",EDGE,"E72.0");var subQ14=sQuery(id+"F12.wireOp",EDGE,"E72.1");var subQ16=sQuery(id+"F12.wireOp",EDGE,"E74.1");var subQ18=sQuery(id+"F12.wireOp",EDGE,"E74.8");Q0=qUnion([makeQuery(id+"F12.imprint","IMPRINT",FACE,{"disambiguationData":[TD([[makeQuery(id+"F12.imprint","IMPRINT",EDGE,{"derivedFrom":subQ7}),1.0]])]}),makeQuery(id+"F12.imprint","IMPRINT",FACE,{"disambiguationData":[TD([[makeQuery(id+"F12.imprint","IMPRINT",EDGE,{"derivedFrom":subQ14}),1.0]])]}),makeQuery(id+"F12.imprint","IMPRINT",FACE,{"disambiguationData":[TD([[makeQuery(id+"F12.imprint","IMPRINT",EDGE,{"derivedFrom":subQ16}),1.0]])]}),makeQuery(id+"F12.imprint","IMPRINT",FACE,{"disambiguationData":[TD([[makeQuery(id+"F12.imprint","IMPRINT",EDGE,{"derivedFrom":subQ18}),-1.0]])]})]);}
            var Q1;
            Q1=makeQuery(id+"F5.boolean.opBoolean","SPLIT",FACE,{"disambiguationData":[TD([makeQuery(id+"F5.opExtrude","SWEPT_FACE",FACE,{"disambiguationData":[OSD([sQuery(id+"F4.wireOp",EDGE,"E41")])]})])],"derivedFrom":makeQuery(id+"F3.boolean.opBoolean","COPY",FACE,{"derivedFrom":makeQuery(id+"F3.opExtrude","CAP_FACE",FACE,{"disambiguationData":[OSD([sQuery(id+"F0.wireOp",EDGE,"E25.0"),sQuery(id+"F0.wireOp",EDGE,"E25.1"),sQuery(id+"F0.wireOp",EDGE,"E25.2"),sQuery(id+"F0.wireOp",EDGE,"E25.3"),sQuery(id+"F0.wireOp",EDGE,"E25.4"),sQuery(id+"F0.wireOp",EDGE,"E25.5"),sQuery(id+"F0.wireOp",EDGE,"E25.6"),sQuery(id+"F0.wireOp",EDGE,"E25.7")])],"isStart":false})})});
            extrude(context, id + "F13", {"entities" : qUnion([Q0]), "operationType" : NewBodyOperationType.REMOVE, "endBound" : BoundingType.UP_TO_SURFACE, "endBoundEntityFace" : qUnion([Q1]), "depth" : 25 * mm});
        }
        {
            var Q0;
            Q0=makeQuery(id+"F3.boolean.opBoolean","COPY",EDGE,{"derivedFrom":makeQuery(id+"F3.opExtrude","CAP_EDGE",EDGE,{"disambiguationData":[OSD([sQuery(id+"F0.wireOp",EDGE,"E25.6")])],"isStart":false})});
            var Q1;
            Q1=makeQuery(id+"F8.boolean.opBoolean","INTERSECT",EDGE,{"derivedFrom":[makeQuery(id+"F5.opExtrude","SWEPT_FACE",FACE,{"disambiguationData":[OSD([sQuery(id+"F4.wireOp",EDGE,"E30")])]}),makeQuery(id+"F8.opExtrude","CAP_FACE",FACE,{"disambiguationData":[OSD([sQuery(id+"F7.wireOp",EDGE,"E67")])],"isStart":false})]});
            var Q2;
            Q2=makeQuery(id+"F8.boolean.opBoolean","INTERSECT",EDGE,{"disambiguationData":[OD(1.0)],"derivedFrom":[makeQuery(id+"F5.opExtrude","SWEPT_FACE",FACE,{"disambiguationData":[OSD([sQuery(id+"F4.wireOp",EDGE,"E30")])]}),makeQuery(id+"F8.opExtrude","SWEPT_FACE",FACE,{"disambiguationData":[OSD([sQuery(id+"F7.wireOp",EDGE,"E67")])]})]});
            var Q3;
            {var subQ0=sQuery(id+"F4.wireOp",EDGE,"E30");Q3=makeQuery(id+"F8.boolean.opBoolean","SPLIT",EDGE,{"disambiguationData":[TD([makeQuery(id+"F5.opExtrude","SWEPT_FACE",FACE,{"disambiguationData":[OSD([sQuery(id+"F4.wireOp",EDGE,"E35.filletArc")])]})])],"derivedFrom":makeQuery(id+"F5.opExtrude","CAP_EDGE",EDGE,{"disambiguationData":[OSD([subQ0])],"isStart":false})});}
            var Q4;
            {var subQ0=sQuery(id+"F0.wireOp",EDGE,"E25.7");var subQ1=sQuery(id+"F0.wireOp",EDGE,"E25.1");var subQ2=sQuery(id+"F0.wireOp",EDGE,"E25.6");var subQ3=sQuery(id+"F0.wireOp",EDGE,"E25.5");var subQ4=sQuery(id+"F0.wireOp",EDGE,"E25.4");var subQ5=sQuery(id+"F0.wireOp",EDGE,"E25.0");var subQ6=sQuery(id+"F0.wireOp",EDGE,"E25.2");var subQ7=sQuery(id+"F0.wireOp",EDGE,"E25.3");Q4=makeQuery(id+"F8.boolean.opBoolean","INTERSECT",EDGE,{"derivedFrom":[makeQuery(id+"F5.boolean.opBoolean","SPLIT",FACE,{"disambiguationData":[TD([makeQuery(id+"F2.opExtrude","SWEPT_FACE",FACE,{"disambiguationData":[OSD([subQ5])]})])],"derivedFrom":makeQuery(id+"F3.boolean.opBoolean","COPY",FACE,{"derivedFrom":makeQuery(id+"F3.opExtrude","CAP_FACE",FACE,{"disambiguationData":[OSD([subQ5,subQ1,subQ6,subQ7,subQ4,subQ3,subQ2,subQ0])],"isStart":false})})}),makeQuery(id+"F8.opExtrude","SWEPT_FACE",FACE,{"disambiguationData":[OSD([sQuery(id+"F7.wireOp",EDGE,"E67")])]})]});}
            var Q5;
            Q5=makeQuery(id+"F8.boolean.opBoolean","INTERSECT",EDGE,{"disambiguationData":[OD(0.0)],"derivedFrom":[makeQuery(id+"F5.opExtrude","SWEPT_FACE",FACE,{"disambiguationData":[OSD([sQuery(id+"F4.wireOp",EDGE,"E30")])]}),makeQuery(id+"F8.opExtrude","SWEPT_FACE",FACE,{"disambiguationData":[OSD([sQuery(id+"F7.wireOp",EDGE,"E67")])]})]});
            fillet(context, id + "F14", {"entities" : qUnion([Q0, Q1, Q2, Q3, Q4, Q5]), "radius" : 3 * mm, "tangentPropagation" : true, "allowEdgeOverflow" : false});
        }
        {
            var Q0;
            Q0=makeQuery(id+"F1.opExtrude","CAP_EDGE",EDGE,{"disambiguationData":[OSD([sQuery(id+"F0.wireOp",EDGE,"E1.bottom")])],"isStart":false});
            fillet(context, id + "F15", {"entities" : qUnion([Q0]), "radius" : 2 * mm, "tangentPropagation" : true, "allowEdgeOverflow" : false});
        }
        {
            var Q0;
            {var subQ0=sQuery(id+"F0.wireOp",EDGE,"E22.filletArc");var subQ1=sQuery(id+"F0.wireOp",EDGE,"E7");var subQ2=sQuery(id+"F0.wireOp",EDGE,"E6");var subQ3=sQuery(id+"F0.wireOp",EDGE,"E5");var subQ4=sQuery(id+"F0.wireOp",EDGE,"E4");var subQ5=sQuery(id+"F0.wireOp",EDGE,"E1.bottom");var subQ6=sQuery(id+"F0.wireOp",EDGE,"E21.filletArc");var subQ7=sQuery(id+"F0.wireOp",EDGE,"E1.top");var subQ8=sQuery(id+"F0.wireOp",EDGE,"E1.left");var subQ9=sQuery(id+"F0.wireOp",EDGE,"E1.right");var subQ10=sQuery(id+"F0.wireOp",EDGE,"E23.filletArc");var subQ11=sQuery(id+"F0.wireOp",EDGE,"E24.filletArc");Q0=makeQuery(id+"F2.boolean.opBoolean","SPLIT",FACE,{"disambiguationData":[TD([makeQuery(id+"F1.opExtrude","SWEPT_FACE",FACE,{"disambiguationData":[OSD([subQ5])]})])],"derivedFrom":makeQuery(id+"F1.opExtrude","CAP_FACE",FACE,{"disambiguationData":[OSD([subQ5,subQ7,subQ8,subQ9,subQ4,subQ3,subQ2,subQ1,subQ6,subQ0,subQ10,subQ11])],"isStart":true})});}
            var sketch = newSketch(context, id + "F16", { "sketchPlane" : qUnion([Q0])});
            skCircle(sketch, "E79", {"center": v(0, 104.25) * mm, "radius": 6 * mm});
            skArc(sketch, "E80", {"start": v(-15, 103.9) * mm, "mid": v(-0.17, 119.25) * mm, "end": v(15, 104.25) * mm});
            skLineSegment(sketch, "E81", {"start": v(-15, 103.9) * mm, "end": v(-15, 92.25) * mm});
            skLineSegment(sketch, "E82", {"start": v(15, 104.25) * mm, "end": v(15, 92.6) * mm});
            skLineSegment(sketch, "E83", {"start": v(-15, 92.25) * mm, "end": v(-33, 74.25) * mm});
            skLineSegment(sketch, "E84", {"start": v(15, 92.6) * mm, "end": v(33.34, 74.25) * mm});
            skLineSegment(sketch, "E85", {"start": v(0, 104.25) * mm, "end": v(0, 74.25) * mm, "construction": true});
            skLineSegment(sketch, "E86", {"start": v(-74.25, 0) * mm, "end": v(74.25, 0) * mm});
            skLineSegment(sketch, "E87.MirrorCS", {"start": v(-15, -92.25) * mm, "end": v(-33, -74.25) * mm});
            skLineSegment(sketch, "E88.MirrorCS", {"start": v(-15, -103.9) * mm, "end": v(-15, -92.25) * mm});
            skArc(sketch, "E89.MirrorCS", {"start": v(-15, -103.9) * mm, "mid": v(-0.17, -119.25) * mm, "end": v(15, -104.25) * mm});
            skLineSegment(sketch, "E90.MirrorCS", {"start": v(15, -92.6) * mm, "end": v(33.34, -74.25) * mm});
            skLineSegment(sketch, "E91.MirrorCS", {"start": v(15, -104.25) * mm, "end": v(15, -92.6) * mm});
            skCircle(sketch, "E92.MirrorC", {"center": v(0, -104.25) * mm, "radius": 6 * mm});
            skSolve(sketch);
        }
        {
            var Q0;
            Q0=makeQuery(id+"F16.imprint","IMPRINT",FACE,{"disambiguationData":[TD([[makeQuery(id+"F16.imprint","IMPRINT",EDGE,{"derivedFrom":sQuery(id+"F16.wireOp",EDGE,"E79")}),-1.0]])]});
            var Q1;
            {var subQ0=sQuery(id+"F16.wireOp",EDGE,"E87.MirrorCS");Q1=makeQuery(id+"F16.imprint","IMPRINT",FACE,{"disambiguationData":[TD([[makeQuery(id+"F16.imprint","IMPRINT",EDGE,{"derivedFrom":subQ0}),-1.0]])]});}
            var Q2;
            Q2=makeQuery(id+"F16.imprint","IMPRINT",FACE,{"disambiguationData":[TD([[makeQuery(id+"F16.imprint","IMPRINT",EDGE,{"derivedFrom":makeQuery(id+"F1.opExtrude","CAP_EDGE",EDGE,{"disambiguationData":[OSD([sQuery(id+"F0.wireOp",EDGE,"E4")])],"isStart":true})}),-1.0]])]});
            var Q3;
            Q3=makeQuery(id+"F16.imprint","IMPRINT",FACE,{"disambiguationData":[TD([[makeQuery(id+"F16.imprint","IMPRINT",EDGE,{"derivedFrom":makeQuery(id+"F1.opExtrude","CAP_EDGE",EDGE,{"disambiguationData":[OSD([sQuery(id+"F0.wireOp",EDGE,"E6")])],"isStart":true})}),-1.0]])]});
            var Q4;
            Q4=makeQuery(id+"F2.opExtrude","CAP_FACE",FACE,{"disambiguationData":[OSD([sQuery(id+"F0.wireOp",EDGE,"E12"),sQuery(id+"F0.wireOp",EDGE,"E13"),sQuery(id+"F0.wireOp",EDGE,"E14"),sQuery(id+"F0.wireOp",EDGE,"E15"),sQuery(id+"F0.wireOp",EDGE,"E17.filletArc"),sQuery(id+"F0.wireOp",EDGE,"E18.filletArc"),sQuery(id+"F0.wireOp",EDGE,"E19.filletArc"),sQuery(id+"F0.wireOp",EDGE,"E20.filletArc"),sQuery(id+"F0.wireOp",EDGE,"E25.0"),sQuery(id+"F0.wireOp",EDGE,"E25.1"),sQuery(id+"F0.wireOp",EDGE,"E25.2"),sQuery(id+"F0.wireOp",EDGE,"E25.3"),sQuery(id+"F0.wireOp",EDGE,"E25.4"),sQuery(id+"F0.wireOp",EDGE,"E25.5"),sQuery(id+"F0.wireOp",EDGE,"E25.6"),sQuery(id+"F0.wireOp",EDGE,"E25.7")])],"isStart":false});
            extrude(context, id + "F17", {"entities" : qUnion([Q0, Q1, Q2, Q3]), "endBound" : BoundingType.UP_TO_SURFACE, "endBoundEntityFace" : qUnion([Q4]), "depth" : 25 * mm});
        }
    });
